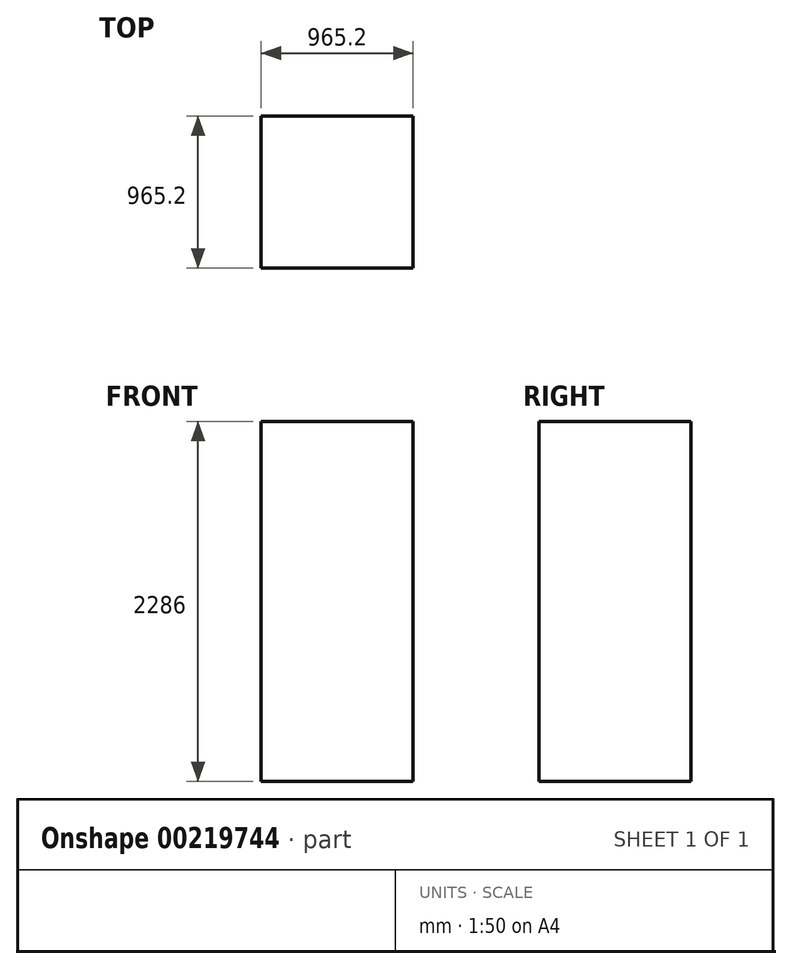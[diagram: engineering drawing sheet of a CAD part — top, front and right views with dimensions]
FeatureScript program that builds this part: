
annotation { "Feature Type Name" : "Feature", "Feature Type Description" : "" }
export const myFeature = defineFeature(function(context is Context, id is Id, definition is map)
    precondition{}
    {
        {
            var Q0;
            Q0=qCreatedBy(makeId("Front.planeOp"),FACE);
            var sketch = newSketch(context, id + "F0", { "sketchPlane" : qUnion([Q0])});
            skLineSegment(sketch, "E0.bottom", {"start": v(0, 0) * mm, "end": v(965.2, 0) * mm});
            skLineSegment(sketch, "E0.top", {"start": v(0, 2286) * mm, "end": v(965.2, 2286) * mm});
            skLineSegment(sketch, "E0.left", {"start": v(0, 0) * mm, "end": v(0, 2286) * mm});
            skLineSegment(sketch, "E0.right", {"start": v(965.2, 0) * mm, "end": v(965.2, 2286) * mm});
            skSolve(sketch);
        }
        {
            var Q0;
            Q0=makeQuery(id+"F0.imprint","IMPRINT",FACE,{"disambiguationData":[TD([[makeQuery(id+"F0.imprint","IMPRINT",EDGE,{"derivedFrom":sQuery(id+"F0.wireOp",EDGE,"E0.bottom")}),1.0]])]});
            extrude(context, id + "F1", {"entities" : qUnion([Q0]), "oppositeDirection" : true, "depth" : 965.2 * mm});
        }
    });
